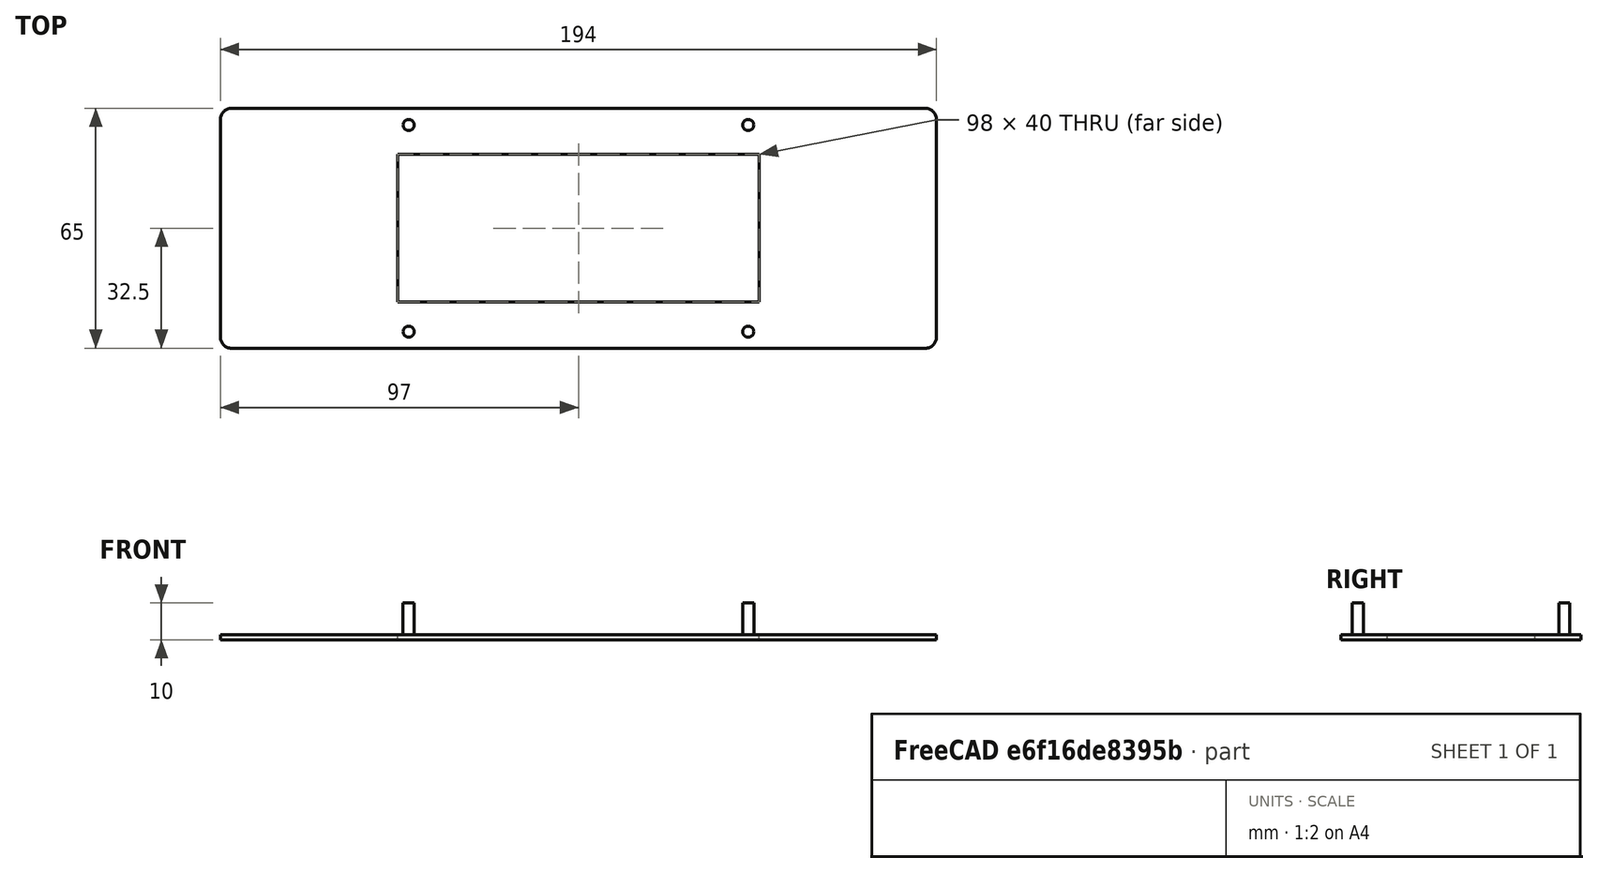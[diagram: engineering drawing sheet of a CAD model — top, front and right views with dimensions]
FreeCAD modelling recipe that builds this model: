
FCSTD DOCUMENT  (FreeCAD 0.20R29603 (Git))
Label: Facade-v3
License: All rights reserved
LicenseURL: http://en.wikipedia.org/wiki/All_rights_reserved
objects: PartDesign::Fillet×4, Sketcher::SketchObject×2, PartDesign::Pad×2, PartDesign::Body×1, Mesh::Feature×1
note: 15 computed .brp shape members not serialized (recipe doc carries the construction recipe); baked Part::Feature solids carry a one-line shape summary decoded from their .brp

FEATURE [Sketcher::SketchObject] Sketch
  FullyConstrained = true
  MapMode = 5
  Support = -> [XY_Plane]
  sketch-geometry (8):
    g0: LineSegment StartX=-97 StartY=32.5 StartZ=0 EndX=97 EndY=32.5 EndZ=0
    g1: LineSegment StartX=97 StartY=32.5 StartZ=0 EndX=97 EndY=-32.5 EndZ=0
    g2: LineSegment StartX=97 StartY=-32.5 StartZ=0 EndX=-97 EndY=-32.5 EndZ=0
    g3: LineSegment StartX=-97 StartY=-32.5 StartZ=0 EndX=-97 EndY=32.5 EndZ=0
    g4: LineSegment StartX=-49 StartY=20 StartZ=0 EndX=49 EndY=20 EndZ=0
    g5: LineSegment StartX=49 StartY=20 StartZ=0 EndX=49 EndY=-20 EndZ=0
    g6: LineSegment StartX=49 StartY=-20 StartZ=0 EndX=-49 EndY=-20 EndZ=0
    g7: LineSegment StartX=-49 StartY=-20 StartZ=0 EndX=-49 EndY=20 EndZ=0
  constraints (22):
    c: Coincident(g0,g1)
    c: Coincident(g1,g2)
    c: Coincident(g2,g3)
    c: Coincident(g3,g0)
    c: Horizontal(g0)
    c: Horizontal(g2)
    c: Vertical(g1)
    c: Vertical(g3)
    c: Symmetric(g0,g1,g-1)
    c: DistanceX(g0,g0) = 194
    c: DistanceY(g3,g3) = 65
    c: Coincident(g4,g5)
    c: Coincident(g5,g6)
    c: Coincident(g6,g7)
    c: Coincident(g7,g4)
    c: Horizontal(g4)
    c: Horizontal(g6)
    c: Vertical(g5)
    c: Vertical(g7)
    c: Symmetric(g4,g5,g-1)
    c: DistanceX(g6,g6) = 98
    c: DistanceY(g5,g5) = 40
FEATURE [PartDesign::Pad] Pad  label="Support"
  Direction = (0,0,1)
  Length = 1.4
  Length2 = 10
  Profile = -> Sketch
  ReferenceAxis = -> Sketch [N_Axis]
  Type = 0
FEATURE [Sketcher::SketchObject] Sketch001
  FullyConstrained = true
  MapMode = 5
  Support = -> [XY_Plane]
  sketch-geometry (4):
    g0: Circle CenterX=-46 CenterY=28 CenterZ=0 NormalX=0 NormalY=0 NormalZ=1 AngleXU=0 Radius=1.5
    g1: Circle CenterX=-46 CenterY=-28 CenterZ=0 NormalX=0 NormalY=0 NormalZ=1 AngleXU=0 Radius=1.5
    g2: Circle CenterX=46 CenterY=28 CenterZ=0 NormalX=0 NormalY=0 NormalZ=1 AngleXU=0 Radius=1.5
    g3: Circle CenterX=46 CenterY=-28 CenterZ=0 NormalX=0 NormalY=0 NormalZ=1 AngleXU=0 Radius=1.5
  constraints (12):
    c: DistanceX(g0,g-1) = 46
    c: DistanceX(g1,g-1) = 46
    c: DistanceX(g-1,g2) = 46
    c: DistanceX(g-1,g3) = 46
    c: DistanceY(g-1,g0) = 28
    c: DistanceY(g1,g-1) = 28
    c: DistanceY(g-1,g2) = 28
    c: DistanceY(g3,g-1) = 28
    c: Diameter(g1) = 3
    c: Diameter(g0) = 3
    c: Diameter(g2) = 3
    c: Diameter(g3) = 3
FEATURE [PartDesign::Pad] Pad001  label="Pitons"
  BaseFeature = -> Pad
  Direction = (0,0,1)
  Length = 10
  Length2 = 10
  Profile = -> Sketch001
  ReferenceAxis = -> Sketch001 [N_Axis]
  Type = 0
FEATURE [PartDesign::Fillet] Fillet
  Base = -> Pad001 [Edge5]
  BaseFeature = -> Pad001
  Radius = 3
  SupportTransform = false
  UseAllEdges = false
FEATURE [PartDesign::Fillet] Fillet001
  Base = -> Fillet [Edge31]
  BaseFeature = -> Fillet
  Radius = 3
  SupportTransform = false
  UseAllEdges = false
FEATURE [PartDesign::Fillet] Fillet002
  Base = -> Fillet001 [Edge22]
  BaseFeature = -> Fillet001
  Radius = 3
  SupportTransform = false
  UseAllEdges = false
FEATURE [PartDesign::Fillet] Fillet003
  Base = -> Fillet002 [Edge23]
  BaseFeature = -> Fillet002
  Radius = 3
  SupportTransform = false
  UseAllEdges = false
FEATURE [PartDesign::Body] Body
  Group = -> [Sketch,Pad,Sketch001,Pad001,Fillet,Fillet001,Fillet002,Fillet003]
  Origin = -> Origin
  Tip = -> Fillet003
FEATURE [Mesh::Feature] Mesh  label="Body (Meshed)"
